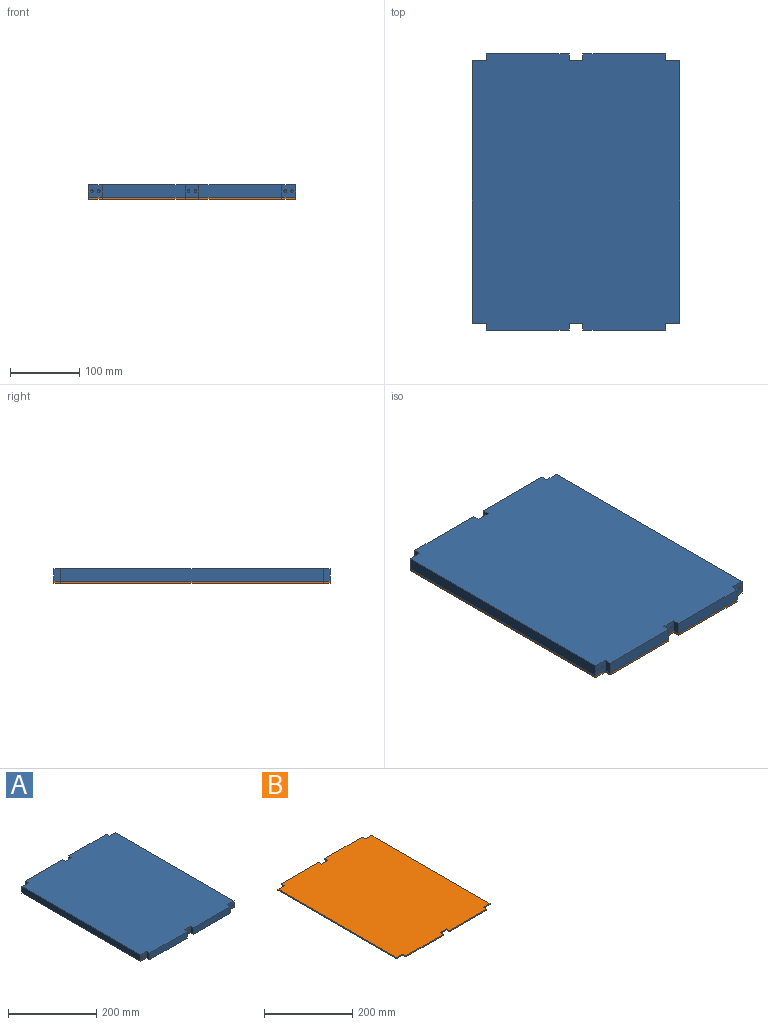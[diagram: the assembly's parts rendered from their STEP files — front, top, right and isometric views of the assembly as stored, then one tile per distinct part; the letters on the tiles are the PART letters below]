
ASSEMBLY  parts=2 mates=1
PART A: 46 faces, bbox 300x400x18 mm
  f0: plane 120x18mm, normal (0,1,0), area 2160mm2, adj f6,f7,f27,f31
  f1: plane 120x18mm, normal (0,1,0), area 2160mm2, adj f6,f7,f29,f32
  f2: plane 380x18mm, normal (-1,0,0), area 6840mm2, adj f6,f7,f11,f30
  f3: plane 120x18mm, normal (0,-1,0), area 2160mm2, adj f6,f7,f8,f12
  f4: plane 120x18mm, normal (0,-1,0), area 2160mm2, adj f6,f7,f9,f14
  f5: plane 380x18mm, normal (1,0,0), area 6840mm2, adj f6,f7,f13,f33
  f6: plane 400x300mm, normal (0,0,1), area 118800mm2, adj f0,f1,f2,f3,f4,f5,f8,f9
  f7: plane 400x300mm, normal (0,0,-1), area 118800mm2, adj f0,f1,f2,f3,f4,f5,f8,f9
  f8: plane 18x10mm, normal (1,0,0), area 180mm2, adj f3,f6,f7,f10
  f9: plane 18x10mm, normal (-1,0,0), area 180mm2, adj f4,f6,f7,f10
  f10: plane 20x18mm, normal (0,-1,0), area 334.9mm2, adj f6,f7,f8,f9,f24,f26
  f11: plane 20x18mm, normal (0,-1,0), area 334.9mm2, adj f2,f6,f7,f12,f20,f22
  f12: plane 18x10mm, normal (-1,0,0), area 180mm2, adj f3,f6,f7,f11
  f13: plane 20x18mm, normal (0,-1,0), area 334.9mm2, adj f5,f6,f7,f14,f16,f18
  f14: plane 18x10mm, normal (1,0,0), area 180mm2, adj f4,f6,f7,f13
  f15: cone r=0mm half-angle=59deg, axis (0,-1,0), area 14.7mm2, adj f16
  f16: cylinder r=2mm len=30mm, axis (0,-1,0), area 377mm2, adj f13,f15
  f17: cone r=0mm half-angle=59deg, axis (0,-1,0), area 14.7mm2, adj f18
  f18: cylinder r=2mm len=30mm, axis (0,-1,0), area 377mm2, adj f13,f17
  f19: cone r=0mm half-angle=59deg, axis (0,-1,0), area 14.7mm2, adj f20
  f20: cylinder r=2mm len=30mm, axis (0,-1,0), area 377mm2, adj f11,f19
  f21: cone r=0mm half-angle=59deg, axis (0,-1,0), area 14.7mm2, adj f22
  f22: cylinder r=2mm len=30mm, axis (0,-1,0), area 377mm2, adj f11,f21
  f23: cone r=0mm half-angle=59deg, axis (0,-1,0), area 14.7mm2, adj f24
  f24: cylinder r=2mm len=30mm, axis (0,-1,0), area 377mm2, adj f10,f23
  f25: cone r=0mm half-angle=59deg, axis (0,-1,0), area 14.7mm2, adj f26
  f26: cylinder r=2mm len=30mm, axis (0,-1,0), area 377mm2, adj f10,f25
  f27: plane 18x10mm, normal (1,0,0), area 180mm2, adj f0,f6,f7,f28
  f28: plane 20x18mm, normal (0,1,0), area 334.9mm2, adj f6,f7,f27,f29,f43,f45
  f29: plane 18x10mm, normal (-1,0,0), area 180mm2, adj f1,f6,f7,f28
  f30: plane 20x18mm, normal (0,1,0), area 334.9mm2, adj f2,f6,f7,f31,f39,f41
  f31: plane 18x10mm, normal (-1,0,0), area 180mm2, adj f0,f6,f7,f30
  f32: plane 18x10mm, normal (1,0,0), area 180mm2, adj f1,f6,f7,f33
  f33: plane 20x18mm, normal (0,1,0), area 334.9mm2, adj f5,f6,f7,f32,f35,f37
  f34: cone r=0mm half-angle=59deg, axis (0,1,0), area 14.7mm2, adj f35
  f35: cylinder r=2mm len=30mm, axis (0,1,0), area 377mm2, adj f33,f34
  f36: cone r=0mm half-angle=59deg, axis (0,1,0), area 14.7mm2, adj f37
  f37: cylinder r=2mm len=30mm, axis (0,1,0), area 377mm2, adj f33,f36
  f38: cone r=0mm half-angle=59deg, axis (0,1,0), area 14.7mm2, adj f39
  f39: cylinder r=2mm len=30mm, axis (0,1,0), area 377mm2, adj f30,f38
  f40: cone r=0mm half-angle=59deg, axis (0,1,0), area 14.7mm2, adj f41
  f41: cylinder r=2mm len=30mm, axis (0,1,0), area 377mm2, adj f30,f40
  f42: cone r=0mm half-angle=59deg, axis (0,1,0), area 14.7mm2, adj f43
  f43: cylinder r=2mm len=30mm, axis (0,1,0), area 377mm2, adj f28,f42
  f44: cone r=0mm half-angle=59deg, axis (0,1,0), area 14.7mm2, adj f45
  f45: cylinder r=2mm len=30mm, axis (0,1,0), area 377mm2, adj f28,f44
PART B: 22 faces, bbox 300x400x3 mm
  f0: plane 120x3mm, normal (0,1,0), area 360mm2, adj f6,f7,f15,f19
  f1: plane 120x3mm, normal (0,1,0), area 360mm2, adj f6,f7,f17,f20
  f2: plane 380x3mm, normal (-1,0,0), area 1140mm2, adj f6,f7,f11,f18
  f3: plane 120x3mm, normal (0,-1,0), area 360mm2, adj f6,f7,f8,f12
  f4: plane 120x3mm, normal (0,-1,0), area 360mm2, adj f6,f7,f9,f14
  f5: plane 380x3mm, normal (1,0,0), area 1140mm2, adj f6,f7,f13,f21
  f6: plane 400x300mm, normal (0,0,1), area 118800mm2, adj f0,f1,f2,f3,f4,f5,f8,f9
  f7: plane 400x300mm, normal (0,0,-1), area 118800mm2, adj f0,f1,f2,f3,f4,f5,f8,f9
  f8: plane 10x3mm, normal (1,0,0), area 30mm2, adj f3,f6,f7,f10
  f9: plane 10x3mm, normal (-1,0,0), area 30mm2, adj f4,f6,f7,f10
  f10: plane 20x3mm, normal (0,-1,0), area 60mm2, adj f6,f7,f8,f9
  f11: plane 20x3mm, normal (0,-1,0), area 60mm2, adj f2,f6,f7,f12
  f12: plane 10x3mm, normal (-1,0,0), area 30mm2, adj f3,f6,f7,f11
  f13: plane 20x3mm, normal (0,-1,0), area 60mm2, adj f5,f6,f7,f14
  f14: plane 10x3mm, normal (1,0,0), area 30mm2, adj f4,f6,f7,f13
  f15: plane 10x3mm, normal (1,0,0), area 30mm2, adj f0,f6,f7,f16
  f16: plane 20x3mm, normal (0,1,0), area 60mm2, adj f6,f7,f15,f17
  f17: plane 10x3mm, normal (-1,0,0), area 30mm2, adj f1,f6,f7,f16
  f18: plane 20x3mm, normal (0,1,0), area 60mm2, adj f2,f6,f7,f19
  f19: plane 10x3mm, normal (-1,0,0), area 30mm2, adj f0,f6,f7,f18
  f20: plane 10x3mm, normal (1,0,0), area 30mm2, adj f1,f6,f7,f21
  f21: plane 20x3mm, normal (0,1,0), area 60mm2, adj f5,f6,f7,f20
PLACE A at identity
PLACE B t=(0,0,-3)mm
MATE fastened B.f6 <-> A.f7  axis (0,0,1) through (0,0,0)mm
